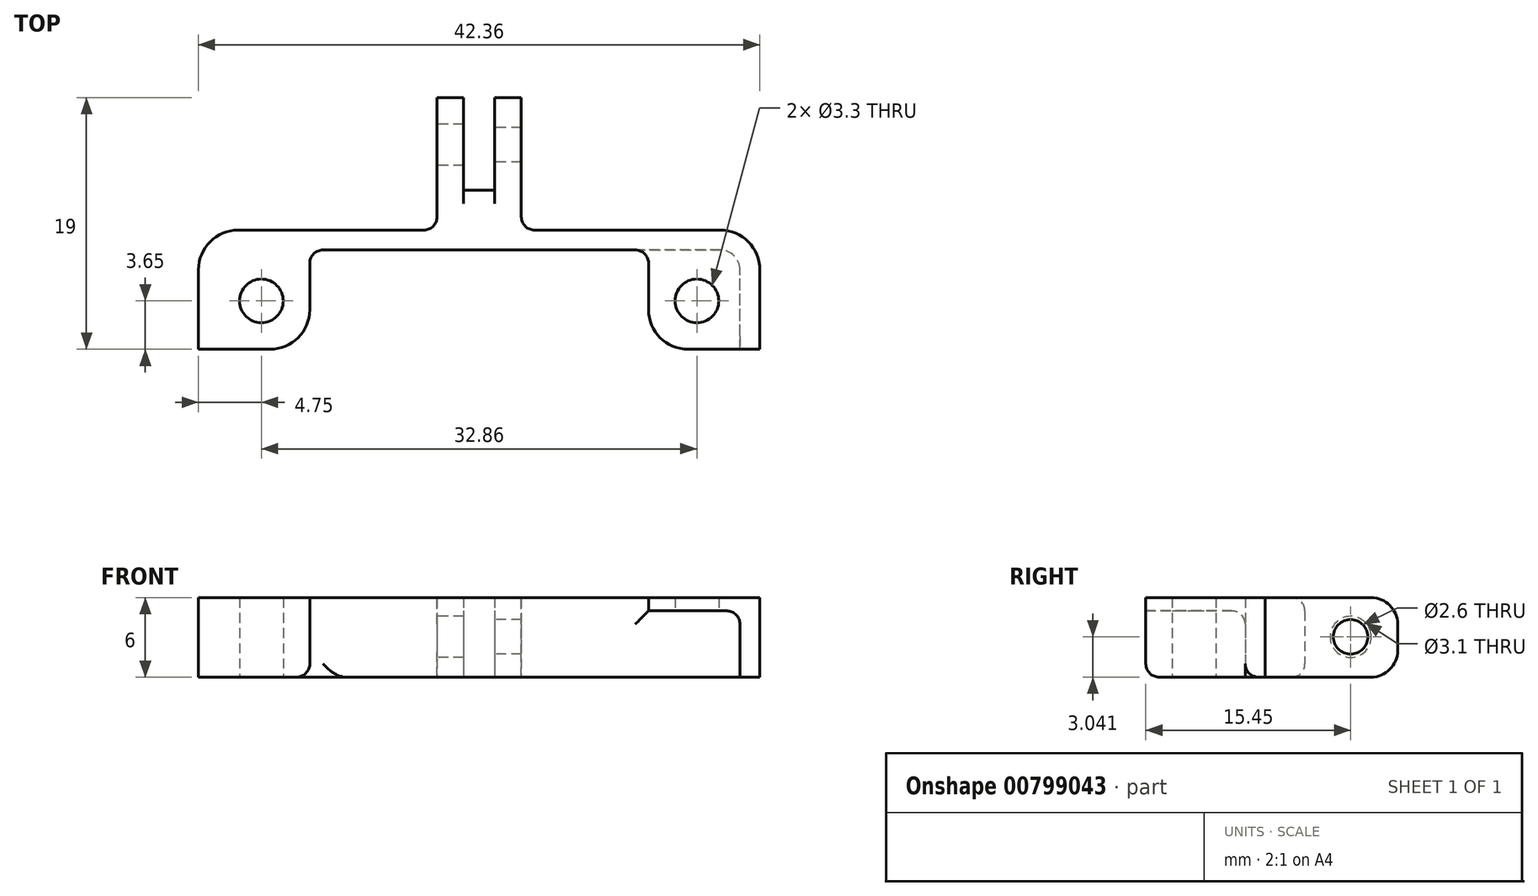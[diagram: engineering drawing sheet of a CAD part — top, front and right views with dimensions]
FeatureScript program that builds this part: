
annotation { "Feature Type Name" : "Feature", "Feature Type Description" : "" }
export const myFeature = defineFeature(function(context is Context, id is Id, definition is map)
    precondition{}
    {
        {
            var Q0;
            Q0=qCreatedBy(makeId("Top.planeOp"),FACE);
            var sketch = newSketch(context, id + "F0", { "sketchPlane" : qUnion([Q0])});
            skLineSegment(sketch, "E0", {"start": v(0, 0) * mm, "end": v(1.18, 0) * mm});
            skLineSegment(sketch, "E1", {"start": v(1.18, 0) * mm, "end": v(1.18, 7) * mm});
            skLineSegment(sketch, "E2", {"start": v(1.18, 7) * mm, "end": v(3.18, 7) * mm});
            skLineSegment(sketch, "E3", {"start": v(3.18, 7) * mm, "end": v(3.18, 0) * mm});
            skLineSegment(sketch, "E4", {"start": v(3.18, 0) * mm, "end": v(3.18, -3) * mm});
            skLineSegment(sketch, "E5", {"start": v(3.18, -3) * mm, "end": v(18.18, -3) * mm});
            skLineSegment(sketch, "E6", {"start": v(21.18, -6) * mm, "end": v(21.18, -12) * mm});
            skPoint(sketch, "E7.visualSharp", {"position": v(21.18, -3) * mm});
            skArc(sketch, "E7.filletArc", {"start": v(21.18, -6) * mm, "mid": v(20.3, -3.88) * mm, "end": v(18.18, -3) * mm});
            skLineSegment(sketch, "E8", {"start": v(21.18, -12) * mm, "end": v(19.68, -12) * mm});
            skLineSegment(sketch, "E9", {"start": v(19.68, -12) * mm, "end": v(19.68, -6) * mm});
            skLineSegment(sketch, "E10", {"start": v(0, 0) * mm, "end": v(0, -12) * mm, "construction": true});
            skLineSegment(sketch, "E11", {"start": v(0, -4.5) * mm, "end": v(18.18, -4.5) * mm});
            skPoint(sketch, "E12.visualSharp", {"position": v(19.68, -4.5) * mm});
            skArc(sketch, "E12.filletArc", {"start": v(19.68, -6) * mm, "mid": v(19.24, -4.94) * mm, "end": v(18.18, -4.5) * mm});
            skLineSegment(sketch, "E13", {"start": v(12.78, -4.5) * mm, "end": v(12.78, -9) * mm});
            skLineSegment(sketch, "E14", {"start": v(15.78, -12) * mm, "end": v(19.68, -12) * mm});
            skPoint(sketch, "E15.visualSharp", {"position": v(12.78, -12) * mm});
            skArc(sketch, "E15.filletArc", {"start": v(12.78, -9) * mm, "mid": v(13.66, -11.12) * mm, "end": v(15.78, -12) * mm});
            skCircle(sketch, "E16", {"center": v(16.43, -8.35) * mm, "radius": 1.65 * mm});
            skLineSegment(sketch, "E17.MirrorCS", {"start": v(0, 0) * mm, "end": v(-1.18, 0) * mm});
            skLineSegment(sketch, "E18.MirrorCS", {"start": v(-1.18, 0) * mm, "end": v(-1.18, 7) * mm});
            skLineSegment(sketch, "E19.MirrorCS", {"start": v(-1.18, 7) * mm, "end": v(-3.18, 7) * mm});
            skLineSegment(sketch, "E20.MirrorCS", {"start": v(-3.18, 7) * mm, "end": v(-3.18, 0) * mm});
            skLineSegment(sketch, "E21.MirrorCS", {"start": v(-3.18, 0) * mm, "end": v(-3.18, -3) * mm});
            skLineSegment(sketch, "E22.MirrorCS", {"start": v(-3.18, -3) * mm, "end": v(-18.18, -3) * mm});
            skArc(sketch, "E23.MirrorCS", {"start": v(-21.18, -6) * mm, "mid": v(-20.3, -3.88) * mm, "end": v(-18.18, -3) * mm});
            skArc(sketch, "E24.MirrorCS", {"start": v(-12.78, -9) * mm, "mid": v(-13.66, -11.12) * mm, "end": v(-15.78, -12) * mm});
            skCircle(sketch, "E25.MirrorC", {"center": v(-16.43, -8.35) * mm, "radius": 1.65 * mm});
            skLineSegment(sketch, "E26.MirrorCS", {"start": v(-15.78, -12) * mm, "end": v(-19.68, -12) * mm});
            skLineSegment(sketch, "E27.MirrorCS", {"start": v(-12.78, -4.5) * mm, "end": v(-12.78, -9) * mm});
            skLineSegment(sketch, "E28.MirrorCS", {"start": v(-19.68, -12) * mm, "end": v(-19.68, -6) * mm});
            skPoint(sketch, "E29.MirrorP", {"position": v(-12.78, -12) * mm});
            skArc(sketch, "E30.MirrorCS", {"start": v(-19.68, -6) * mm, "mid": v(-19.24, -4.94) * mm, "end": v(-18.18, -4.5) * mm});
            skPoint(sketch, "E31.MirrorP", {"position": v(-19.68, -4.5) * mm});
            skLineSegment(sketch, "E32.MirrorCS", {"start": v(0, -4.5) * mm, "end": v(-18.18, -4.5) * mm});
            skLineSegment(sketch, "E33.MirrorCS", {"start": v(-21.18, -6) * mm, "end": v(-21.18, -12) * mm});
            skLineSegment(sketch, "E34.MirrorCS", {"start": v(-21.18, -12) * mm, "end": v(-19.68, -12) * mm});
            skSolve(sketch);
        }
        {
            var Q0;
            Q0 = qSketchRegion(id + "F0", true);
            extrude(context, id + "F1", {"entities" : qUnion([Q0]), "depth" : 6 * mm, "offsetDistance" : 25 * mm});
        }
        {
            var Q0;
            Q0=makeQuery(id+"F0.imprint","IMPRINT",FACE,{"disambiguationData":[TD([[makeQuery(id+"F0.imprint","IMPRINT",EDGE,{"derivedFrom":sQuery(id+"F0.wireOp",EDGE,"E24.MirrorCS")}),-1.0]])]});
            var Q1;
            Q1=makeQuery(id+"F0.imprint","IMPRINT",FACE,{"disambiguationData":[TD([[makeQuery(id+"F0.imprint","IMPRINT",EDGE,{"derivedFrom":sQuery(id+"F0.wireOp",EDGE,"E9")}),1.0]])]});
            extrude(context, id + "F2", {"entities" : qUnion([Q0, Q1]), "operationType" : NewBodyOperationType.REMOVE, "depth" : 5 * mm, "offsetDistance" : 25 * mm});
        }
        {
            var Q0;
            Q0=makeQuery(id+"F1.opExtrude","SWEPT_FACE",FACE,{"disambiguationData":[OSD([sQuery(id+"F0.wireOp",EDGE,"E20.MirrorCS"),sQuery(id+"F0.wireOp",EDGE,"E21.MirrorCS")])]});
            var sketch = newSketch(context, id + "F3", { "sketchPlane" : qUnion([Q0])});
            skCircle(sketch, "E35", {"center": v(-3.45, 3.04) * mm, "radius": 1.3 * mm});
            skCircle(sketch, "E36", {"center": v(-3.45, 3.04) * mm, "radius": 1.55 * mm});
            skSolve(sketch);
        }
        {
            var Q0;
            Q0=makeQuery(id+"F1.opExtrude","CAP_EDGE",EDGE,{"disambiguationData":[OSD([sQuery(id+"F0.wireOp",EDGE,"E19.MirrorCS")])],"isStart":false});
            var Q1;
            Q1=makeQuery(id+"F1.opExtrude","CAP_EDGE",EDGE,{"disambiguationData":[OSD([sQuery(id+"F0.wireOp",EDGE,"E2")])],"isStart":false});
            var Q2;
            Q2=makeQuery(id+"F1.opExtrude","CAP_EDGE",EDGE,{"disambiguationData":[OSD([sQuery(id+"F0.wireOp",EDGE,"E2")])],"isStart":true});
            var Q3;
            Q3=makeQuery(id+"F1.opExtrude","CAP_EDGE",EDGE,{"disambiguationData":[OSD([sQuery(id+"F0.wireOp",EDGE,"E19.MirrorCS")])],"isStart":true});
            fillet(context, id + "F4", {"entities" : qUnion([Q0, Q1, Q2, Q3]), "radius" : 2 * mm, "tangentPropagation" : true, "allowEdgeOverflow" : false});
        }
        {
            var Q0;
            Q0=makeQuery(id+"F3.imprint","IMPRINT",FACE,{"disambiguationData":[TD([[makeQuery(id+"F3.imprint","IMPRINT",EDGE,{"derivedFrom":sQuery(id+"F3.wireOp",EDGE,"E35")}),1.0]])]});
            extrude(context, id + "F5", {"entities" : qUnion([Q0]), "operationType" : NewBodyOperationType.REMOVE, "oppositeDirection" : true, "depth" : 7 * mm, "offsetDistance" : 25 * mm});
        }
        {
            var Q0;
            Q0=makeQuery(id+"F3.imprint","IMPRINT",FACE,{"disambiguationData":[TD([[makeQuery(id+"F3.imprint","IMPRINT",EDGE,{"derivedFrom":sQuery(id+"F3.wireOp",EDGE,"E35")}),-1.0]])]});
            extrude(context, id + "F6", {"entities" : qUnion([Q0]), "operationType" : NewBodyOperationType.REMOVE, "oppositeDirection" : true, "depth" : 3 * mm, "offsetDistance" : 25 * mm});
        }
        {
            var Q0;
            Q0=makeQuery(id+"F2.boolean.opBoolean","COPY",EDGE,{"derivedFrom":makeQuery(id+"F2.opExtrude","CAP_EDGE",EDGE,{"disambiguationData":[OSD([sQuery(id+"F0.wireOp",EDGE,"E28.MirrorCS")])],"isStart":false})});
            var Q1;
            Q1=makeQuery(id+"F2.boolean.opBoolean","COPY",EDGE,{"derivedFrom":makeQuery(id+"F2.opExtrude","CAP_EDGE",EDGE,{"disambiguationData":[OSD([sQuery(id+"F0.wireOp",EDGE,"E11")])],"isStart":false})});
            var Q2;
            Q2=makeQuery(id+"F1.opExtrude","SWEPT_EDGE",EDGE,{"disambiguationData":[OSD([sQuery(id+"F0.wireOp",EDGE,"E11"),sQuery(id+"F0.wireOp",EDGE,"E13")])]});
            var Q3;
            Q3=makeQuery(id+"F1.opExtrude","SWEPT_EDGE",EDGE,{"disambiguationData":[OSD([sQuery(id+"F0.wireOp",EDGE,"E27.MirrorCS"),sQuery(id+"F0.wireOp",EDGE,"E32.MirrorCS")])]});
            var Q4;
            Q4=makeQuery(id+"F1.opExtrude","CAP_EDGE",EDGE,{"disambiguationData":[OSD([sQuery(id+"F0.wireOp",EDGE,"E26.MirrorCS"),sQuery(id+"F0.wireOp",EDGE,"E34.MirrorCS")])],"isStart":true});
            var Q5;
            Q5=makeQuery(id+"F1.opExtrude","CAP_EDGE",EDGE,{"disambiguationData":[OSD([sQuery(id+"F0.wireOp",EDGE,"E8"),sQuery(id+"F0.wireOp",EDGE,"E14")])],"isStart":true});
            var Q6;
            Q6=makeQuery(id+"F1.opExtrude","SWEPT_EDGE",EDGE,{"disambiguationData":[OSD([sQuery(id+"F0.wireOp",EDGE,"E4"),sQuery(id+"F0.wireOp",EDGE,"E5")])]});
            var Q7;
            Q7=makeQuery(id+"F1.opExtrude","SWEPT_EDGE",EDGE,{"disambiguationData":[OSD([sQuery(id+"F0.wireOp",EDGE,"E21.MirrorCS"),sQuery(id+"F0.wireOp",EDGE,"E22.MirrorCS")])]});
            var Q8;
            Q8=makeQuery(id+"F1.opExtrude","CAP_EDGE",EDGE,{"disambiguationData":[OSD([sQuery(id+"F0.wireOp",EDGE,"E0"),sQuery(id+"F0.wireOp",EDGE,"E17.MirrorCS")])],"isStart":false});
            var Q9;
            Q9=makeQuery(id+"F1.opExtrude","CAP_EDGE",EDGE,{"disambiguationData":[OSD([sQuery(id+"F0.wireOp",EDGE,"E0"),sQuery(id+"F0.wireOp",EDGE,"E17.MirrorCS")])],"isStart":true});
            fillet(context, id + "F7", {"entities" : qUnion([Q0, Q1, Q2, Q3, Q4, Q5, Q6, Q7, Q8, Q9]), "radius" : 1 * mm, "tangentPropagation" : true, "allowEdgeOverflow" : false});
        }
    });
